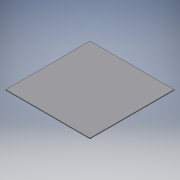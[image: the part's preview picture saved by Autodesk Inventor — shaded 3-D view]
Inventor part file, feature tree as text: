
AUTODESK INVENTOR PART (.ipt)
format: ipt  version: 2016 SP1 (Build 200210100, 210)  size: 87,552 bytes
history: native  units: mm
features: extrude x1, sketch x1
ambient origin geometry x8: Origin, YZ Plane, XZ Plane, XY Plane, X Axis, Y Axis, Z Axis, Center Point
bodies: Solid1 (feature_tree)
feature tree (2):
  extrude  "Extrusion1"  Depth=215.0mm
  sketch  "Sketch1"  dims[d0=215.0mm d1=215.0mm d2=107.5mm d3=107.5mm d4=2.0mm d5=0.0mm]
